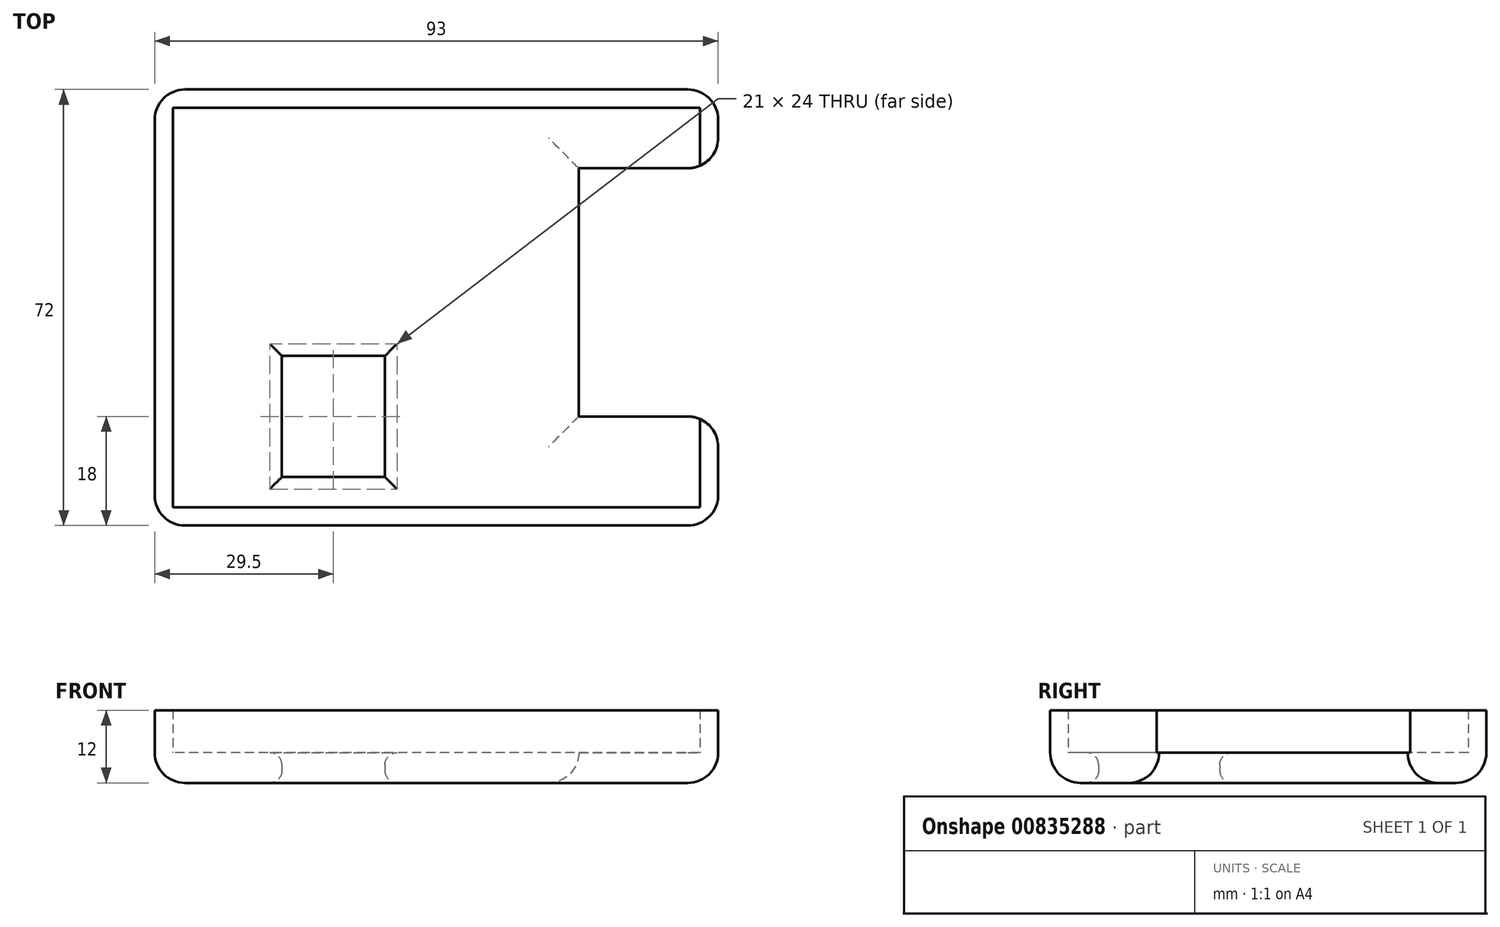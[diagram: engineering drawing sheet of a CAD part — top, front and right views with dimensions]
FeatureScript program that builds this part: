
annotation { "Feature Type Name" : "Feature", "Feature Type Description" : "" }
export const myFeature = defineFeature(function(context is Context, id is Id, definition is map)
    precondition{}
    {
        {
            var Q0;
            Q0=qCreatedBy(makeId("Top.planeOp"),FACE);
            var sketch = newSketch(context, id + "F0", { "sketchPlane" : qUnion([Q0])});
            skLineSegment(sketch, "E0.bottom", {"start": v(43.5, 33) * mm, "end": v(-43.5, 33) * mm});
            skLineSegment(sketch, "E0.top", {"start": v(43.5, -33) * mm, "end": v(-43.5, -33) * mm});
            skLineSegment(sketch, "E0.left", {"start": v(43.5, 33) * mm, "end": v(43.5, -33) * mm});
            skLineSegment(sketch, "E0.right", {"start": v(-43.5, 33) * mm, "end": v(-43.5, -33) * mm});
            skPoint(sketch, "E0.middle", {"position": v(0, 0) * mm});
            skLineSegment(sketch, "E1.bottom", {"start": v(46.5, 36) * mm, "end": v(-46.5, 36) * mm});
            skLineSegment(sketch, "E1.top", {"start": v(46.5, -36) * mm, "end": v(-46.5, -36) * mm});
            skLineSegment(sketch, "E1.left", {"start": v(46.5, 36) * mm, "end": v(46.5, -36) * mm});
            skLineSegment(sketch, "E1.right", {"start": v(-46.5, 36) * mm, "end": v(-46.5, -36) * mm});
            skLineSegment(sketch, "E2.bottom", {"start": v(-25.5, -8) * mm, "end": v(-8.5, -8) * mm});
            skLineSegment(sketch, "E2.top", {"start": v(-25.5, -28) * mm, "end": v(-8.5, -28) * mm});
            skLineSegment(sketch, "E2.left", {"start": v(-25.5, -8) * mm, "end": v(-25.5, -28) * mm});
            skLineSegment(sketch, "E2.right", {"start": v(-8.5, -8) * mm, "end": v(-8.5, -28) * mm});
            skLineSegment(sketch, "E3.bottom", {"start": v(23.5, 23) * mm, "end": v(46.5, 23) * mm});
            skLineSegment(sketch, "E3.top", {"start": v(23.5, -18) * mm, "end": v(46.5, -18) * mm});
            skLineSegment(sketch, "E3.left", {"start": v(23.5, 23) * mm, "end": v(23.5, -18) * mm});
            skLineSegment(sketch, "E3.right", {"start": v(46.5, 23) * mm, "end": v(46.5, -18) * mm});
            skSolve(sketch);
        }
        {
            var Q0;
            {var subQ7=sQuery(id+"F0.wireOp",EDGE,"E0.bottom");Q0=makeQuery(id+"F0.imprint","IMPRINT",FACE,{"disambiguationData":[TD([[makeQuery(id+"F0.imprint","IMPRINT",EDGE,{"derivedFrom":subQ7}),-1.0]])]});}
            extrude(context, id + "F1", {"entities" : qUnion([Q0]), "depth" : 12 * mm, "offsetDistance" : 25 * mm});
        }
        {
            var Q0;
            {var subQ4=sQuery(id+"F0.wireOp",EDGE,"E0.bottom");Q0=makeQuery(id+"F0.imprint","IMPRINT",FACE,{"disambiguationData":[TD([[makeQuery(id+"F0.imprint","IMPRINT",EDGE,{"derivedFrom":subQ4}),1.0]])]});}
            extrude(context, id + "F2", {"entities" : qUnion([Q0]), "operationType" : NewBodyOperationType.ADD, "depth" : 5 * mm, "offsetDistance" : 25 * mm});
        }
        {
            var Q0;
            Q0=makeQuery(id+"F2.opExtrude","CAP_EDGE",EDGE,{"disambiguationData":[OSD([sQuery(id+"F0.wireOp",EDGE,"E3.left")])],"isStart":true});
            var Q1;
            {var subQ0=sQuery(id+"F0.wireOp",EDGE,"E3.top");Q1=makeQuery(id+"F2.boolean.opBoolean","MERGE",EDGE,{"derivedFrom":[makeQuery(id+"F1.opExtrude","CAP_EDGE",EDGE,{"disambiguationData":[OSD([subQ0])],"isStart":true}),makeQuery(id+"F2.opExtrude","CAP_EDGE",EDGE,{"disambiguationData":[OSD([subQ0])],"isStart":true})]});}
            var Q2;
            {var subQ0=sQuery(id+"F0.wireOp",EDGE,"E3.bottom");Q2=makeQuery(id+"F2.boolean.opBoolean","MERGE",EDGE,{"derivedFrom":[makeQuery(id+"F1.opExtrude","CAP_EDGE",EDGE,{"disambiguationData":[OSD([subQ0])],"isStart":true}),makeQuery(id+"F2.opExtrude","CAP_EDGE",EDGE,{"disambiguationData":[OSD([subQ0])],"isStart":true})]});}
            var Q3;
            {var subQ0=sQuery(id+"F0.wireOp",EDGE,"E1.left");Q3=makeQuery(id+"F1.opExtrude","CAP_EDGE",EDGE,{"disambiguationData":[OSD([subQ0]),TDD([makeQuery(id+"F0.imprint","IMPRINT",EDGE,{"disambiguationData":[TD([[makeQuery(id+"F0.imprint","INTERSECT",VERTEX,{"derivedFrom":[sQuery(id+"F0.wireOp",EDGE,"E1.bottom"),subQ0]}),-1.0]])],"derivedFrom":subQ0})])],"isStart":true});}
            var Q4;
            {var subQ0=sQuery(id+"F0.wireOp",EDGE,"E1.left");Q4=makeQuery(id+"F1.opExtrude","CAP_EDGE",EDGE,{"disambiguationData":[OSD([subQ0]),TDD([makeQuery(id+"F0.imprint","IMPRINT",EDGE,{"disambiguationData":[TD([[makeQuery(id+"F0.imprint","INTERSECT",VERTEX,{"derivedFrom":[sQuery(id+"F0.wireOp",EDGE,"E1.top"),subQ0]}),1.0]])],"derivedFrom":subQ0})])],"isStart":true});}
            var Q5;
            Q5=makeQuery(id+"F1.opExtrude","CAP_EDGE",EDGE,{"disambiguationData":[OSD([sQuery(id+"F0.wireOp",EDGE,"E1.top")])],"isStart":true});
            var Q6;
            Q6=makeQuery(id+"F1.opExtrude","CAP_EDGE",EDGE,{"disambiguationData":[OSD([sQuery(id+"F0.wireOp",EDGE,"E1.bottom")])],"isStart":true});
            var Q7;
            Q7=makeQuery(id+"F1.opExtrude","CAP_EDGE",EDGE,{"disambiguationData":[OSD([sQuery(id+"F0.wireOp",EDGE,"E1.right")])],"isStart":true});
            var Q8;
            Q8=makeQuery(id+"F1.opExtrude","SWEPT_EDGE",EDGE,{"disambiguationData":[OSD([sQuery(id+"F0.wireOp",EDGE,"E1.bottom"),sQuery(id+"F0.wireOp",EDGE,"E1.right")])]});
            var Q9;
            Q9=makeQuery(id+"F1.opExtrude","SWEPT_EDGE",EDGE,{"disambiguationData":[OSD([sQuery(id+"F0.wireOp",EDGE,"E1.bottom"),sQuery(id+"F0.wireOp",EDGE,"E1.left")])]});
            var Q10;
            Q10=makeQuery(id+"F1.opExtrude","SWEPT_EDGE",EDGE,{"disambiguationData":[OSD([sQuery(id+"F0.wireOp",EDGE,"E1.top"),sQuery(id+"F0.wireOp",EDGE,"E1.left")])]});
            var Q11;
            Q11=makeQuery(id+"F1.opExtrude","SWEPT_EDGE",EDGE,{"disambiguationData":[OSD([sQuery(id+"F0.wireOp",EDGE,"E1.top"),sQuery(id+"F0.wireOp",EDGE,"E1.right")])]});
            var Q12;
            Q12=makeQuery(id+"F1.opExtrude","SWEPT_EDGE",EDGE,{"disambiguationData":[OSD([sQuery(id+"F0.wireOp",EDGE,"E1.left"),sQuery(id+"F0.wireOp",EDGE,"E3.top")])]});
            var Q13;
            Q13=makeQuery(id+"F1.opExtrude","SWEPT_EDGE",EDGE,{"disambiguationData":[OSD([sQuery(id+"F0.wireOp",EDGE,"E1.left"),sQuery(id+"F0.wireOp",EDGE,"E3.bottom")])]});
            fillet(context, id + "F3", {"entities" : qUnion([Q0, Q1, Q2, Q3, Q4, Q5, Q6, Q7, Q8, Q9, Q10, Q11, Q12, Q13]), "tangentPropagation" : true, "radius" : 5 * mm, "defaultsChanged" : false, "vertexSettings" : [], "allowEdgeOverflow" : false});
        }
        {
            var Q0;
            Q0=makeQuery(id+"F2.opExtrude","CAP_EDGE",EDGE,{"disambiguationData":[OSD([sQuery(id+"F0.wireOp",EDGE,"E2.left")])],"isStart":false});
            var Q1;
            Q1=makeQuery(id+"F2.opExtrude","CAP_EDGE",EDGE,{"disambiguationData":[OSD([sQuery(id+"F0.wireOp",EDGE,"E2.top")])],"isStart":false});
            var Q2;
            Q2=makeQuery(id+"F2.opExtrude","CAP_EDGE",EDGE,{"disambiguationData":[OSD([sQuery(id+"F0.wireOp",EDGE,"E2.bottom")])],"isStart":false});
            var Q3;
            Q3=makeQuery(id+"F2.opExtrude","CAP_EDGE",EDGE,{"disambiguationData":[OSD([sQuery(id+"F0.wireOp",EDGE,"E2.right")])],"isStart":false});
            var Q4;
            Q4=makeQuery(id+"F2.opExtrude","CAP_EDGE",EDGE,{"disambiguationData":[OSD([sQuery(id+"F0.wireOp",EDGE,"E2.bottom")])],"isStart":true});
            var Q5;
            Q5=makeQuery(id+"F2.opExtrude","CAP_EDGE",EDGE,{"disambiguationData":[OSD([sQuery(id+"F0.wireOp",EDGE,"E2.left")])],"isStart":true});
            var Q6;
            Q6=makeQuery(id+"F2.opExtrude","CAP_EDGE",EDGE,{"disambiguationData":[OSD([sQuery(id+"F0.wireOp",EDGE,"E2.top")])],"isStart":true});
            var Q7;
            Q7=makeQuery(id+"F2.opExtrude","CAP_EDGE",EDGE,{"disambiguationData":[OSD([sQuery(id+"F0.wireOp",EDGE,"E2.right")])],"isStart":true});
            fillet(context, id + "F4", {"entities" : qUnion([Q0, Q1, Q2, Q3, Q4, Q5, Q6, Q7]), "tangentPropagation" : true, "radius" : 2 * mm, "defaultsChanged" : true, "vertexSettings" : [], "allowEdgeOverflow" : false});
        }
    });
